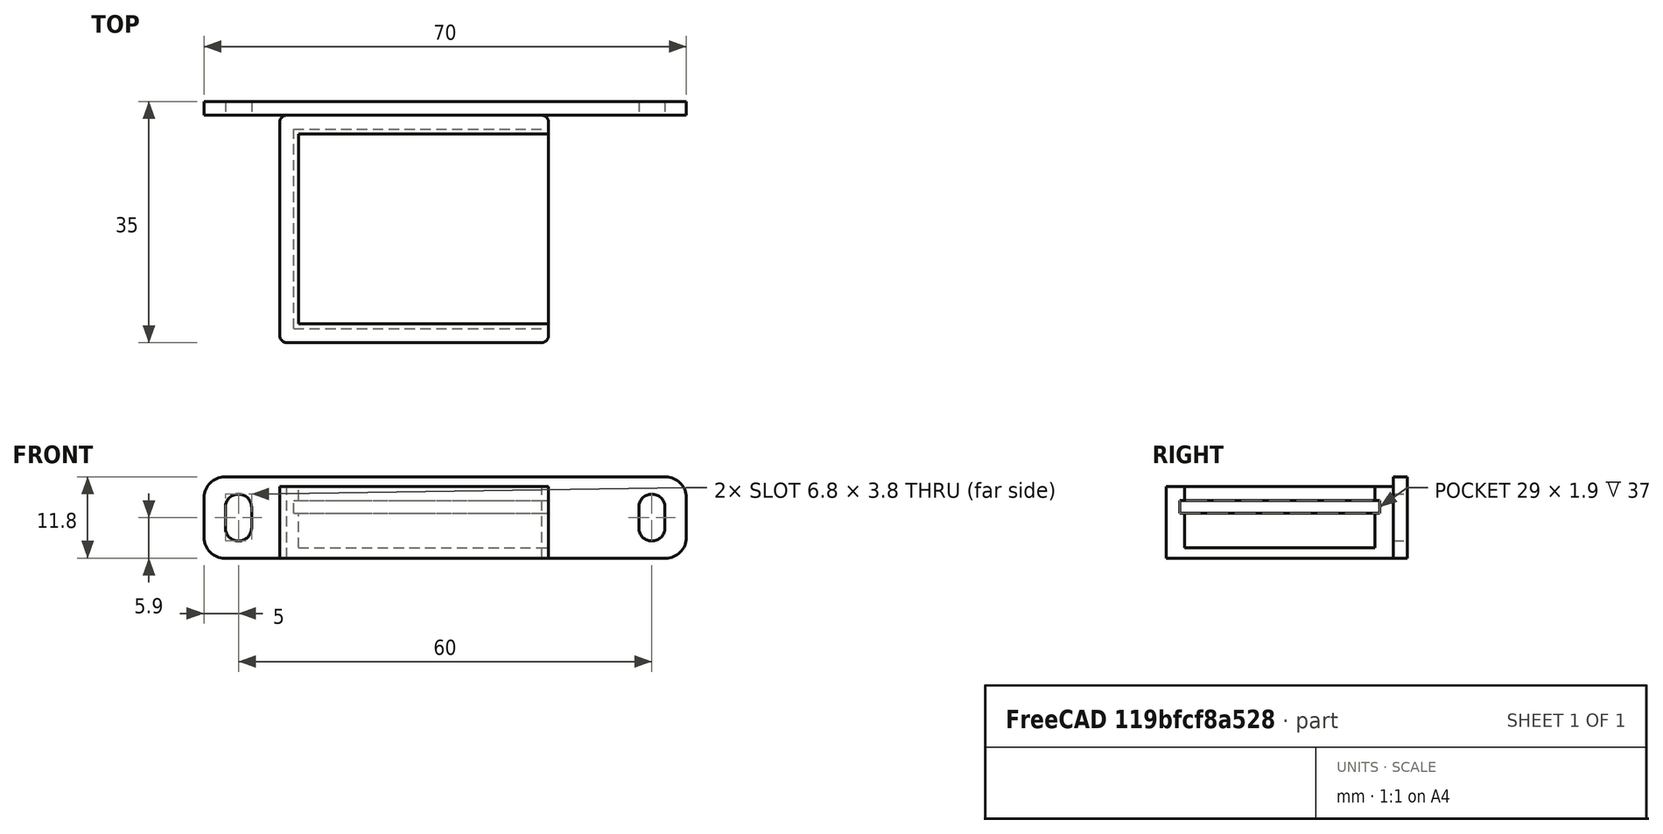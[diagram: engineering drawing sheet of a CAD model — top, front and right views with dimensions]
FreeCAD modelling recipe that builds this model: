
FCSTD DOCUMENT  (FreeCAD 0.20R29410 (Git))
Label: esp32-devkit_48x28
License: FreeArt
LicenseURL: http://artlibre.org/licence/lal
objects: Part::Box×3, Part::MultiFuse×2, Spreadsheet::Sheet×1, Part::Fillet×1, Part::Feature×1, Part::Cut×1, App::Part×1
note: 8 computed .brp shape members not serialized (recipe doc carries the construction recipe); baked Part::Feature solids carry a one-line shape summary decoded from their .brp

FEATURE [Spreadsheet::Sheet] Spreadsheet  label="p"
  cells = A1=pcb_x; B1(pcb_x)=37; A2=pcb_y; B2(pcb_y)=29; A3=pcb_z; B3(pcb_z)=1.9; A4=pcb_under; B4(pcb_under)=5; A5=side_wall; B5(side_wall)=2; A6=pcb_side_lane; B6(pcb_side_lane)=0.7; A7=bottom_wall; B7(bottom_wall)=1.5; A8=pcb_above; B8(pcb_above)=2
FEATURE [Part::Box] Box  label="external cube"
  AttacherType = Attacher::AttachEngine3D
  Height = 10.4
  Length = 39
  Width = 33
  expr: Height = <<p>>.bottom_wall + <<p>>.pcb_under + <<p>>.pcb_z + <<p>>.pcb_above
  expr: Length = <<p>>.pcb_x + <<p>>.side_wall
  expr: Width = <<p>>.pcb_y + 2 * <<p>>.side_wall
FEATURE [Part::Box] Box006  label="internal cube"
  AttacherType = Attacher::AttachEngine3D
  Height = 8.9
  Length = 37.6
  Placement = pos=(2.7,2.7,1.5) rot=(0,0,1;0rad)
  Width = 27.6
  expr: .Placement.Base.x = <<p>>.side_wall + <<p>>.pcb_side_lane
  expr: .Placement.Base.y = <<p>>.side_wall + <<p>>.pcb_side_lane
  expr: .Placement.Base.z = <<p>>.bottom_wall
  expr: Height = <<p>>.pcb_under + <<p>>.pcb_z + <<p>>.pcb_above
  expr: Length = <<p>>.pcb_x - 2 * <<p>>.pcb_side_lane + <<p>>.side_wall
  expr: Width = <<p>>.pcb_y - 2 * <<p>>.pcb_side_lane
FEATURE [Part::Box] Box007  label="pcb extract cube"
  AttacherType = Attacher::AttachEngine3D
  Height = 1.9
  Length = 37
  Placement = pos=(2,2,6.5) rot=(0,0,1;0rad)
  Width = 29
  expr: .Placement.Base.x = <<p>>.side_wall
  expr: .Placement.Base.y = <<p>>.side_wall
  expr: .Placement.Base.z = <<p>>.bottom_wall + <<p>>.pcb_under
  expr: Height = <<p>>.pcb_z
  expr: Length = <<p>>.pcb_x
  expr: Width = <<p>>.pcb_y
FEATURE [Part::MultiFuse] Fusion  label="extract fusion"
  Shapes = -> [Box006,Box007]
FEATURE [Part::Fillet] Fillet  label="external fillet"
  Base = -> Box
  Edges = 4 edges r=1: [Edge1,Edge3,Edge5,Edge7]
FEATURE [Part::Feature] Body002002  label="attach plane x reverse rotated dir002"
  Placement = pos=(-11,35,0) rot=(1,0,0;1.5708rad)
  shape: bbox 70 x 2 x 11.8 mm, 18 faces (baked)
FEATURE [Part::MultiFuse] Fusion001  label="solid fusion"
  Shapes = -> [Fillet,Body002002]
FEATURE [Part::Cut] Cut  label="body cut"
  Base = -> Fusion001
  Tool = -> Fusion
FEATURE [App::Part] Part  label="charger hw pcb box part"
  Group = -> [Box,Fillet,Fusion001,Fusion,Box007,Box006,Cut]
  Origin = -> Origin
